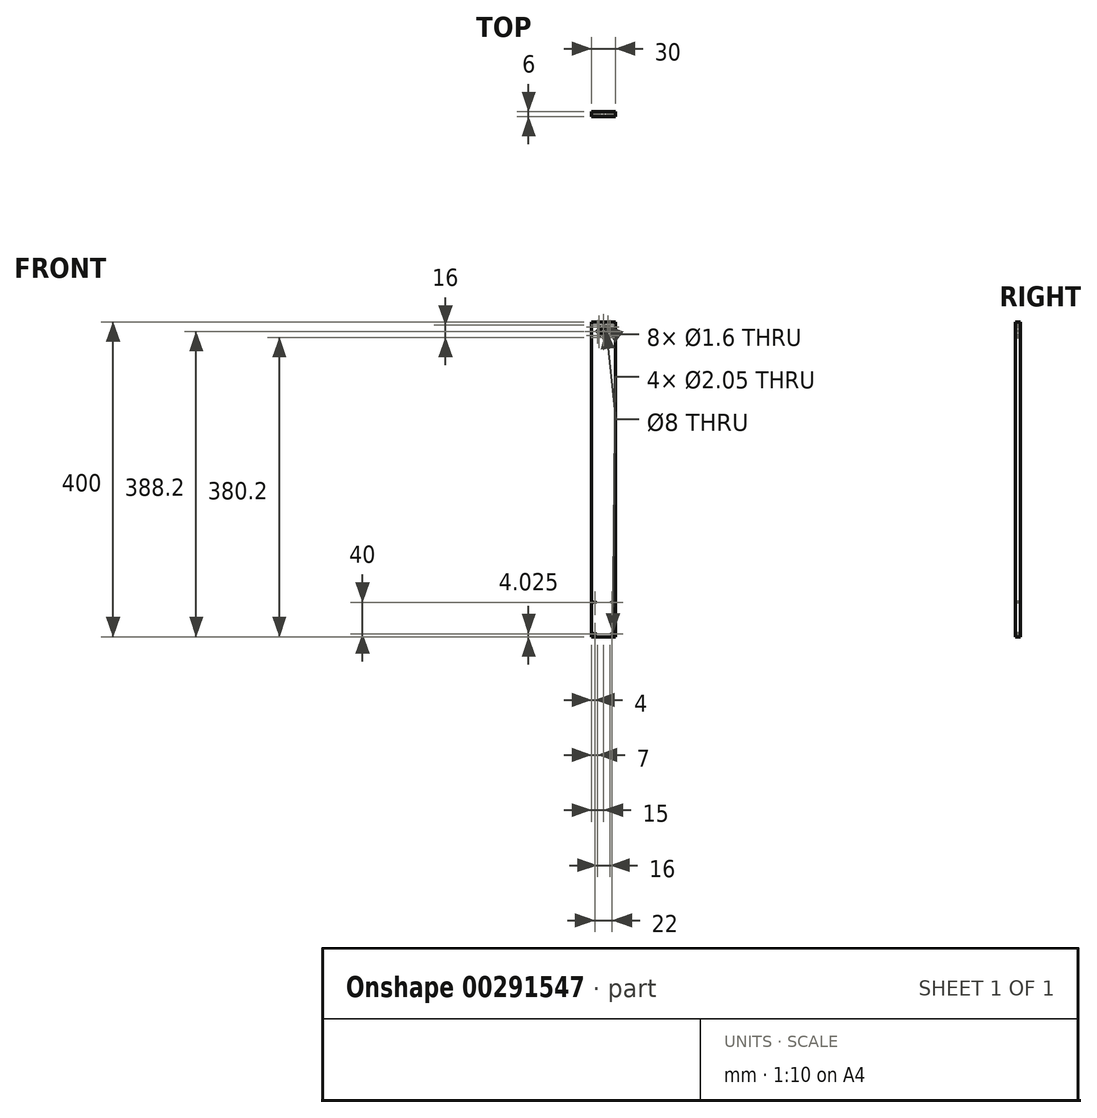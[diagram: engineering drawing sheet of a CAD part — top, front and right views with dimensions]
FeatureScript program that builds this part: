
annotation { "Feature Type Name" : "Feature", "Feature Type Description" : "" }
export const myFeature = defineFeature(function(context is Context, id is Id, definition is map)
    precondition{}
    {
        {
            var Q0;
            Q0=qCreatedBy(makeId("Top.planeOp"),FACE);
            var sketch = newSketch(context, id + "F0", { "sketchPlane" : qUnion([Q0])});
            skLineSegment(sketch, "E0.bottom", {"start": v(-15, 3) * mm, "end": v(15, 3) * mm});
            skLineSegment(sketch, "E0.top", {"start": v(-15, -3) * mm, "end": v(15, -3) * mm});
            skLineSegment(sketch, "E0.left", {"start": v(-15, 3) * mm, "end": v(-15, -3) * mm});
            skLineSegment(sketch, "E0.right", {"start": v(15, 3) * mm, "end": v(15, -3) * mm});
            skSolve(sketch);
        }
        {
            var Q0;
            Q0=qSketchRegion(id+"F0",true);
            extrude(context, id + "F1", {"entities" : qUnion([Q0]), "endBound" : BoundingType.SYMMETRIC, "depth" : 400 * mm, "offsetDistance" : 25 * mm});
        }
        {
            var Q0;
            Q0=makeQuery(id+"F1.opExtrude","SWEPT_FACE",FACE,{"disambiguationData":[OSD([sQuery(id+"F0.wireOp",EDGE,"E0.top")])]});
            var sketch = newSketch(context, id + "F2", { "sketchPlane" : qUnion([Q0])});
            skCircle(sketch, "E1", {"center": v(0, 196.2) * mm, "radius": 0.8 * mm});
            skCircle(sketch, "E2", {"center": v(0, 188.2) * mm, "radius": 4 * mm});
            skCircle(sketch, "E3.1.0", {"center": v(-5.66, 193.86) * mm, "radius": 0.8 * mm});
            skCircle(sketch, "E3.2.0", {"center": v(-8, 188.2) * mm, "radius": 0.8 * mm});
            skCircle(sketch, "E3.3.0", {"center": v(-5.66, 182.54) * mm, "radius": 0.8 * mm});
            skCircle(sketch, "E3.4.0", {"center": v(0, 180.2) * mm, "radius": 0.8 * mm});
            skCircle(sketch, "E3.5.0", {"center": v(5.66, 182.54) * mm, "radius": 0.8 * mm});
            skCircle(sketch, "E3.6.0", {"center": v(8, 188.2) * mm, "radius": 0.8 * mm});
            skCircle(sketch, "E3.7.0", {"center": v(5.66, 193.86) * mm, "radius": 0.8 * mm});
            skCircle(sketch, "E4", {"center": v(11, -195.98) * mm, "radius": 1.02 * mm});
            skCircle(sketch, "E5", {"center": v(11, -155.97) * mm, "radius": 1.02 * mm});
            skCircle(sketch, "E6", {"center": v(-11, -155.97) * mm, "radius": 1.02 * mm});
            skCircle(sketch, "E7", {"center": v(-11, -195.98) * mm, "radius": 1.02 * mm});
            skSolve(sketch);
        }
        {
            var Q0;
            Q0=qSketchRegion(id+"F2",true);
            extrude(context, id + "F3", {"entities" : qUnion([Q0]), "operationType" : NewBodyOperationType.REMOVE, "endBound" : BoundingType.UP_TO_NEXT, "oppositeDirection" : true, "depth" : 25 * mm});
        }
    });
